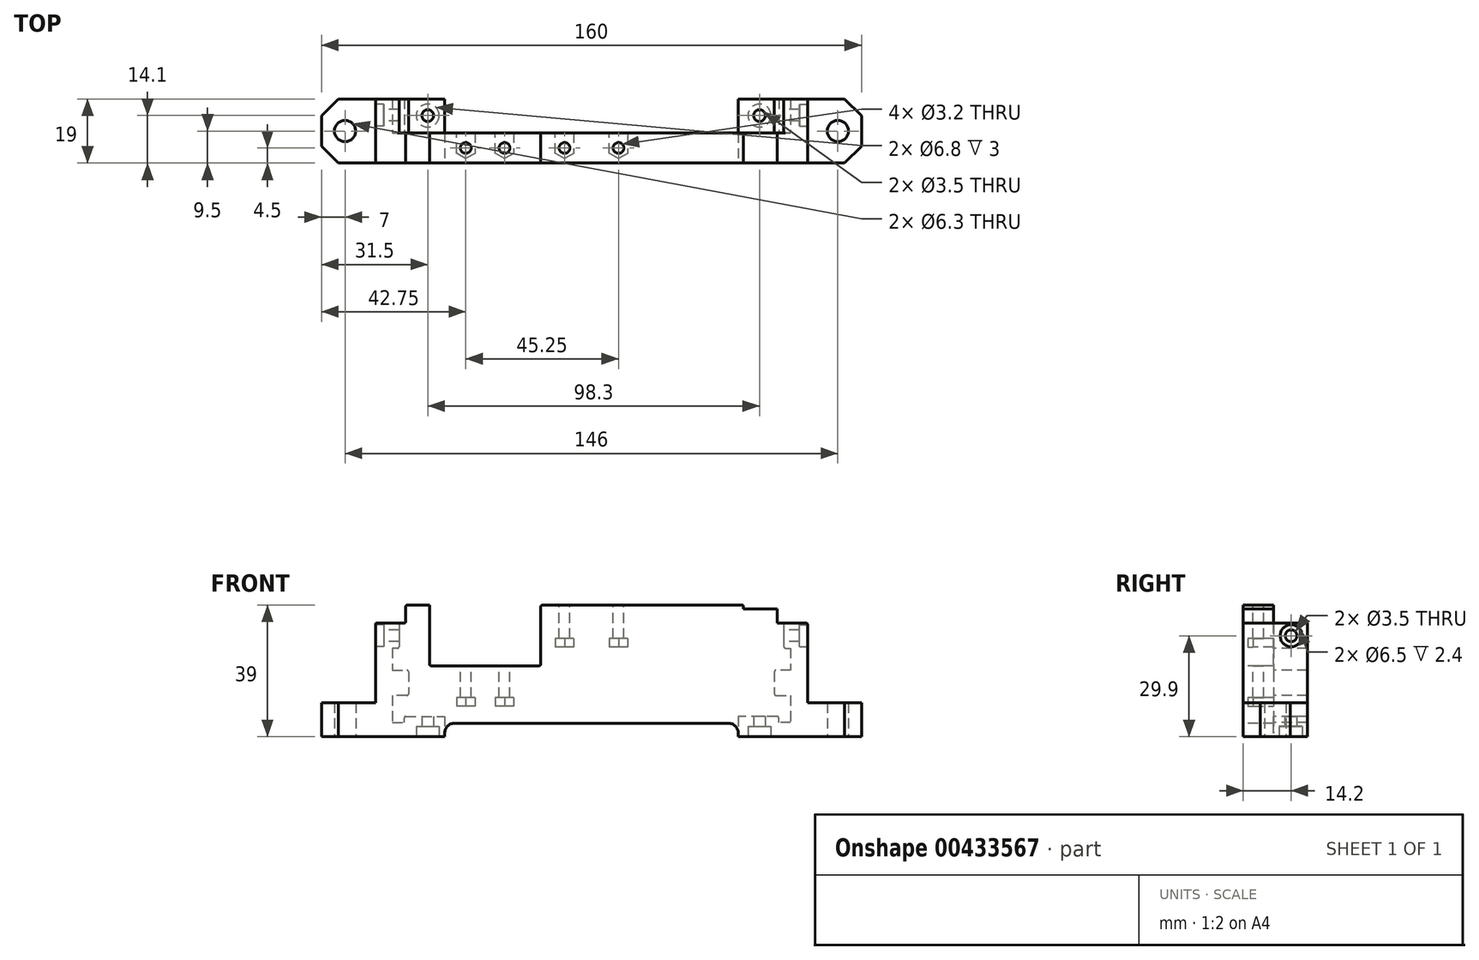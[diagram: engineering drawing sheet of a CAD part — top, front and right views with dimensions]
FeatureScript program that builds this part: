
annotation { "Feature Type Name" : "Feature", "Feature Type Description" : "" }
export const myFeature = defineFeature(function(context is Context, id is Id, definition is map)
    precondition{}
    {
        {
            var Q0;
            Q0=qCreatedBy(makeId("Front.planeOp"),FACE);
            var sketch = newSketch(context, id + "F0", { "sketchPlane" : qUnion([Q0])});
            skLineSegment(sketch, "E0", {"start": v(-64, 27.7) * mm, "end": v(-57.5, 27.7) * mm});
            skLineSegment(sketch, "E1", {"start": v(-57, 27.2) * mm, "end": v(-57, 20.7) * mm});
            skLineSegment(sketch, "E2", {"start": v(-57.5, 20.2) * mm, "end": v(-59, 20.2) * mm});
            skLineSegment(sketch, "E3", {"start": v(-59, 20.2) * mm, "end": v(-59, 13.7) * mm});
            skLineSegment(sketch, "E4", {"start": v(-59, 13.7) * mm, "end": v(-54.7, 13.7) * mm});
            skLineSegment(sketch, "E5", {"start": v(-54.2, 13.2) * mm, "end": v(-54.2, 6.7) * mm});
            skLineSegment(sketch, "E6", {"start": v(-54.7, 6.2) * mm, "end": v(-59, 6.2) * mm});
            skLineSegment(sketch, "E7", {"start": v(-59, 6.2) * mm, "end": v(-59, -1.8) * mm});
            skLineSegment(sketch, "E8", {"start": v(-59, -1.8) * mm, "end": v(-55.5, -1.8) * mm});
            skLineSegment(sketch, "E9", {"start": v(-55.5, -1.8) * mm, "end": v(-55.5, -0.5) * mm});
            skLineSegment(sketch, "E10", {"start": v(-55, 0) * mm, "end": v(-43.5, 0) * mm});
            skLineSegment(sketch, "E11", {"start": v(-43.5, 0) * mm, "end": v(-43.5, -6) * mm});
            skLineSegment(sketch, "E12", {"start": v(-43.5, -6) * mm, "end": v(-64, -6) * mm});
            skLineSegment(sketch, "E13", {"start": v(-64, -6) * mm, "end": v(-64, 27.7) * mm});
            skLineSegment(sketch, "E14", {"start": v(0, 0) * mm, "end": v(0, 39.92) * mm, "construction": true});
            skPoint(sketch, "E15.visualSharp", {"position": v(-54.2, 13.7) * mm});
            skArc(sketch, "E15.filletArc", {"start": v(-54.2, 13.2) * mm, "mid": v(-54.35, 13.55) * mm, "end": v(-54.7, 13.7) * mm});
            skPoint(sketch, "E16.visualSharp", {"position": v(-54.2, 6.2) * mm});
            skArc(sketch, "E16.filletArc", {"start": v(-54.7, 6.2) * mm, "mid": v(-54.35, 6.35) * mm, "end": v(-54.2, 6.7) * mm});
            skPoint(sketch, "E17.visualSharp", {"position": v(-55.5, 0) * mm});
            skArc(sketch, "E17.filletArc", {"start": v(-55, 0) * mm, "mid": v(-55.35, -0.15) * mm, "end": v(-55.5, -0.5) * mm});
            skPoint(sketch, "E18.visualSharp", {"position": v(-57, 27.7) * mm});
            skArc(sketch, "E18.filletArc", {"start": v(-57, 27.2) * mm, "mid": v(-57.15, 27.55) * mm, "end": v(-57.5, 27.7) * mm});
            skPoint(sketch, "E19.visualSharp", {"position": v(-57, 20.2) * mm});
            skArc(sketch, "E19.filletArc", {"start": v(-57.5, 20.2) * mm, "mid": v(-57.15, 20.35) * mm, "end": v(-57, 20.7) * mm});
            skLineSegment(sketch, "E20.MirrorCS", {"start": v(64, -6) * mm, "end": v(64, 27.7) * mm});
            skLineSegment(sketch, "E21.MirrorCS", {"start": v(43.5, -6) * mm, "end": v(64, -6) * mm});
            skLineSegment(sketch, "E22.MirrorCS", {"start": v(43.5, 0) * mm, "end": v(43.5, -6) * mm});
            skLineSegment(sketch, "E23.MirrorCS", {"start": v(55, 0) * mm, "end": v(43.5, 0) * mm});
            skArc(sketch, "E24.MirrorCS", {"start": v(55, 0) * mm, "mid": v(55.35, -0.15) * mm, "end": v(55.5, -0.5) * mm});
            skLineSegment(sketch, "E25.MirrorCS", {"start": v(55.5, -1.8) * mm, "end": v(55.5, -0.5) * mm});
            skLineSegment(sketch, "E26.MirrorCS", {"start": v(59, -1.8) * mm, "end": v(55.5, -1.8) * mm});
            skLineSegment(sketch, "E27.MirrorCS", {"start": v(59, 6.2) * mm, "end": v(59, -1.8) * mm});
            skLineSegment(sketch, "E28.MirrorCS", {"start": v(54.7, 6.2) * mm, "end": v(59, 6.2) * mm});
            skArc(sketch, "E29.MirrorCS", {"start": v(54.7, 6.2) * mm, "mid": v(54.35, 6.35) * mm, "end": v(54.2, 6.7) * mm});
            skLineSegment(sketch, "E30.MirrorCS", {"start": v(54.2, 13.2) * mm, "end": v(54.2, 6.7) * mm});
            skArc(sketch, "E31.MirrorCS", {"start": v(54.2, 13.2) * mm, "mid": v(54.35, 13.55) * mm, "end": v(54.7, 13.7) * mm});
            skLineSegment(sketch, "E32.MirrorCS", {"start": v(59, 13.7) * mm, "end": v(54.7, 13.7) * mm});
            skLineSegment(sketch, "E33.MirrorCS", {"start": v(59, 20.2) * mm, "end": v(59, 13.7) * mm});
            skLineSegment(sketch, "E34.MirrorCS", {"start": v(57.5, 20.2) * mm, "end": v(59, 20.2) * mm});
            skArc(sketch, "E35.MirrorCS", {"start": v(57.5, 20.2) * mm, "mid": v(57.15, 20.35) * mm, "end": v(57, 20.7) * mm});
            skLineSegment(sketch, "E36.MirrorCS", {"start": v(57, 27.2) * mm, "end": v(57, 20.7) * mm});
            skArc(sketch, "E37.MirrorCS", {"start": v(57, 27.2) * mm, "mid": v(57.15, 27.55) * mm, "end": v(57.5, 27.7) * mm});
            skLineSegment(sketch, "E38.MirrorCS", {"start": v(64, 27.7) * mm, "end": v(57.5, 27.7) * mm});
            skSolve(sketch);
        }
        {
            var Q0;
            Q0=makeQuery(id+"F0.imprint","IMPRINT",FACE,{"disambiguationData":[TD([[makeQuery(id+"F0.imprint","IMPRINT",EDGE,{"derivedFrom":sQuery(id+"F0.wireOp",EDGE,"E0")}),-1.0]])]});
            var sketch = newSketch(context, id + "F1", { "sketchPlane" : qUnion([Q0])});
            skLineSegment(sketch, "E39", {"start": v(-64, 27.7) * mm, "end": v(-64, -6) * mm});
            skLineSegment(sketch, "E40", {"start": v(-64, -6) * mm, "end": v(0, -6) * mm});
            skLineSegment(sketch, "E41", {"start": v(-64, 27.7) * mm, "end": v(-55, 27.7) * mm});
            skLineSegment(sketch, "E42", {"start": v(-55, 27.7) * mm, "end": v(-55, 31.9) * mm});
            skLineSegment(sketch, "E43", {"start": v(-55, 31.9) * mm, "end": v(0, 31.9) * mm});
            skLineSegment(sketch, "E44.MirrorCS", {"start": v(55, 31.9) * mm, "end": v(0, 31.9) * mm});
            skLineSegment(sketch, "E45.MirrorCS", {"start": v(64, -6) * mm, "end": v(0, -6) * mm});
            skLineSegment(sketch, "E46.MirrorCS", {"start": v(64, 27.7) * mm, "end": v(64, -6) * mm});
            skLineSegment(sketch, "E47.MirrorCS", {"start": v(64, 27.7) * mm, "end": v(55, 27.7) * mm});
            skLineSegment(sketch, "E48.MirrorCS", {"start": v(55, 27.7) * mm, "end": v(55, 31.9) * mm});
            skSolve(sketch);
        }
        {
            var Q0;
            Q0=qSketchRegion(id+"F1",true);
            extrude(context, id + "F2", {"entities" : qUnion([Q0]), "depth" : 9 * mm});
        }
        {
            var Q0;
            Q0=qSketchRegion(id+"F0",true);
            extrude(context, id + "F3", {"entities" : qUnion([Q0]), "operationType" : NewBodyOperationType.ADD, "oppositeDirection" : true, "depth" : 10 * mm});
        }
        {
            var Q0;
            Q0=makeQuery(id+"F3.boolean.opBoolean","MERGE",FACE,{"derivedFrom":[makeQuery(id+"F2.opExtrude","SWEPT_FACE",FACE,{"disambiguationData":[OSD([sQuery(id+"F1.wireOp",EDGE,"E39")])]}),makeQuery(id+"F3.opExtrude","SWEPT_FACE",FACE,{"disambiguationData":[OSD([sQuery(id+"F0.wireOp",EDGE,"E13")])]})]});
            var sketch = newSketch(context, id + "F4", { "sketchPlane" : qUnion([Q0])});
            skCircle(sketch, "E49", {"center": v(-5.2, 23.9) * mm, "radius": 1.75 * mm});
            skCircle(sketch, "E50", {"center": v(-5.2, 23.9) * mm, "radius": 3.25 * mm});
            skSolve(sketch);
        }
        {
            var Q0;
            Q0=makeQuery(id+"F4.imprint","IMPRINT",FACE,{"disambiguationData":[TD([[makeQuery(id+"F4.imprint","IMPRINT",EDGE,{"derivedFrom":sQuery(id+"F4.wireOp",EDGE,"E49")}),1.0]])]});
            extrude(context, id + "F5", {"entities" : qUnion([Q0]), "operationType" : NewBodyOperationType.REMOVE, "oppositeDirection" : true, "depth" : 158.2 * mm});
        }
        {
            var Q0;
            Q0=makeQuery(id+"F4.imprint","IMPRINT",FACE,{"disambiguationData":[TD([[makeQuery(id+"F4.imprint","IMPRINT",EDGE,{"derivedFrom":sQuery(id+"F4.wireOp",EDGE,"E49")}),-1.0]])]});
            extrude(context, id + "F6", {"entities" : qUnion([Q0]), "operationType" : NewBodyOperationType.REMOVE, "oppositeDirection" : true, "depth" : 2.4 * mm});
        }
        {
            var Q0;
            Q0=makeQuery(id+"F3.boolean.opBoolean","MERGE",FACE,{"derivedFrom":[makeQuery(id+"F2.opExtrude","SWEPT_FACE",FACE,{"disambiguationData":[OSD([sQuery(id+"F1.wireOp",EDGE,"E46.MirrorCS")])]}),makeQuery(id+"F3.opExtrude","SWEPT_FACE",FACE,{"disambiguationData":[OSD([sQuery(id+"F0.wireOp",EDGE,"E20.MirrorCS")])]})]});
            var sketch = newSketch(context, id + "F7", { "sketchPlane" : qUnion([Q0])});
            skCircle(sketch, "E51", {"center": v(5.2, 23.9) * mm, "radius": 3.25 * mm});
            skSolve(sketch);
        }
        {
            var Q0;
            Q0=qSketchRegion(id+"F7",true);
            extrude(context, id + "F8", {"entities" : qUnion([Q0]), "operationType" : NewBodyOperationType.REMOVE, "oppositeDirection" : true, "depth" : 2.4 * mm});
        }
        {
            var Q0;
            Q0=makeQuery(id+"F3.boolean.opBoolean","MERGE",FACE,{"derivedFrom":[makeQuery(id+"F2.opExtrude","SWEPT_FACE",FACE,{"disambiguationData":[OSD([sQuery(id+"F1.wireOp",EDGE,"E40"),sQuery(id+"F1.wireOp",EDGE,"E45.MirrorCS")])]}),makeQuery(id+"F3.opExtrude","SWEPT_FACE",FACE,{"disambiguationData":[OSD([sQuery(id+"F0.wireOp",EDGE,"E12")])]}),makeQuery(id+"F3.opExtrude","SWEPT_FACE",FACE,{"disambiguationData":[OSD([sQuery(id+"F0.wireOp",EDGE,"E21.MirrorCS")])]})]});
            var sketch = newSketch(context, id + "F9", { "sketchPlane" : qUnion([Q0])});
            skCircle(sketch, "E52", {"center": v(49.8, -5.1) * mm, "radius": 1.75 * mm});
            skCircle(sketch, "E53", {"center": v(49.8, -5.1) * mm, "radius": 3.4 * mm});
            skCircle(sketch, "E54", {"center": v(-48.5, -5.1) * mm, "radius": 1.75 * mm});
            skCircle(sketch, "E55", {"center": v(-48.5, -5.1) * mm, "radius": 3.4 * mm});
            skSolve(sketch);
        }
        {
            var Q0;
            Q0=qSketchRegion(id+"F9",true);
            var Q1;
            Q1=makeQuery(id+"F9.imprint","IMPRINT",FACE,{"disambiguationData":[TD([[makeQuery(id+"F9.imprint","IMPRINT",EDGE,{"derivedFrom":sQuery(id+"F9.wireOp",EDGE,"E52")}),1.0]])]});
            extrude(context, id + "F10", {"entities" : qUnion([Q0, Q1]), "operationType" : NewBodyOperationType.REMOVE, "oppositeDirection" : true, "depth" : 3 * mm});
        }
        {
            var Q0;
            Q0=makeQuery(id+"F9.imprint","IMPRINT",FACE,{"disambiguationData":[TD([[makeQuery(id+"F9.imprint","IMPRINT",EDGE,{"derivedFrom":sQuery(id+"F9.wireOp",EDGE,"E52")}),1.0]])]});
            var Q1;
            Q1=makeQuery(id+"F9.imprint","IMPRINT",FACE,{"disambiguationData":[TD([[makeQuery(id+"F9.imprint","IMPRINT",EDGE,{"derivedFrom":sQuery(id+"F9.wireOp",EDGE,"E54")}),1.0]])]});
            extrude(context, id + "F11", {"entities" : qUnion([Q0, Q1]), "operationType" : NewBodyOperationType.REMOVE, "oppositeDirection" : true, "depth" : 25 * mm});
        }
        {
            var Q0;
            Q0=makeQuery(id+"F2.opExtrude","SWEPT_FACE",FACE,{"disambiguationData":[OSD([sQuery(id+"F1.wireOp",EDGE,"E43"),sQuery(id+"F1.wireOp",EDGE,"E44.MirrorCS")])]});
            var sketch = newSketch(context, id + "F12", { "sketchPlane" : qUnion([Q0])});
            skLineSegment(sketch, "E56.bottom", {"start": v(45, -9) * mm, "end": v(-55, -9) * mm});
            skLineSegment(sketch, "E56.top", {"start": v(45, 0) * mm, "end": v(-55, 0) * mm});
            skLineSegment(sketch, "E56.left", {"start": v(45, -9) * mm, "end": v(45, 0) * mm});
            skLineSegment(sketch, "E56.right", {"start": v(-55, -9) * mm, "end": v(-55, 0) * mm});
            skSolve(sketch);
        }
        {
            var Q0;
            Q0=qSketchRegion(id+"F12",true);
            extrude(context, id + "F13", {"entities" : qUnion([Q0]), "operationType" : NewBodyOperationType.ADD, "depth" : 1.1 * mm});
        }
        {
            var Q0;
            Q0=makeQuery(id+"F4.imprint","IMPRINT",FACE,{"disambiguationData":[TD([[makeQuery(id+"F4.imprint","IMPRINT",EDGE,{"derivedFrom":sQuery(id+"F4.wireOp",EDGE,"E50")}),-1.0]])]});
            var sketch = newSketch(context, id + "F14", { "sketchPlane" : qUnion([Q0])});
            skLineSegment(sketch, "E57.bottom", {"start": v(9, -6) * mm, "end": v(-10, -6) * mm});
            skLineSegment(sketch, "E57.top", {"start": v(9, 4) * mm, "end": v(-10, 4) * mm});
            skLineSegment(sketch, "E57.left", {"start": v(9, -6) * mm, "end": v(9, 4) * mm});
            skLineSegment(sketch, "E57.right", {"start": v(-10, -6) * mm, "end": v(-10, 4) * mm});
            skSolve(sketch);
        }
        {
            var Q0;
            Q0=qSketchRegion(id+"F14",true);
            extrude(context, id + "F15", {"entities" : qUnion([Q0]), "operationType" : NewBodyOperationType.ADD, "depth" : 16 * mm});
        }
        {
            var Q0;
            Q0=makeQuery(id+"F15.opExtrude","CAP_EDGE",EDGE,{"disambiguationData":[OSD([sQuery(id+"F14.wireOp",EDGE,"E57.left")])],"isStart":false});
            var Q1;
            Q1=makeQuery(id+"F15.opExtrude","CAP_EDGE",EDGE,{"disambiguationData":[OSD([sQuery(id+"F14.wireOp",EDGE,"E57.right")])],"isStart":false});
            chamfer(context, id + "F16", {"entities" : qUnion([Q0, Q1]), "width" : 5 * mm, "tangentPropagation" : true});
        }
        {
            var Q0;
            Q0=makeQuery(id+"F3.boolean.opBoolean","MERGE",FACE,{"derivedFrom":[makeQuery(id+"F2.opExtrude","SWEPT_FACE",FACE,{"disambiguationData":[OSD([sQuery(id+"F1.wireOp",EDGE,"E46.MirrorCS")])]}),makeQuery(id+"F3.opExtrude","SWEPT_FACE",FACE,{"disambiguationData":[OSD([sQuery(id+"F0.wireOp",EDGE,"E20.MirrorCS")])]})]});
            var sketch = newSketch(context, id + "F17", { "sketchPlane" : qUnion([Q0])});
            skLineSegment(sketch, "E58.bottom", {"start": v(-9, -6) * mm, "end": v(10, -6) * mm});
            skLineSegment(sketch, "E58.top", {"start": v(-9, 4) * mm, "end": v(10, 4) * mm});
            skLineSegment(sketch, "E58.left", {"start": v(-9, -6) * mm, "end": v(-9, 4) * mm});
            skLineSegment(sketch, "E58.right", {"start": v(10, -6) * mm, "end": v(10, 4) * mm});
            skSolve(sketch);
        }
        {
            var Q0;
            Q0=qSketchRegion(id+"F17",true);
            extrude(context, id + "F18", {"entities" : qUnion([Q0]), "operationType" : NewBodyOperationType.ADD, "depth" : 16 * mm});
        }
        {
            var Q0;
            Q0=makeQuery(id+"F18.opExtrude","CAP_EDGE",EDGE,{"disambiguationData":[OSD([sQuery(id+"F17.wireOp",EDGE,"E58.right")])],"isStart":false});
            var Q1;
            Q1=makeQuery(id+"F18.opExtrude","CAP_EDGE",EDGE,{"disambiguationData":[OSD([sQuery(id+"F17.wireOp",EDGE,"E58.left")])],"isStart":false});
            chamfer(context, id + "F19", {"entities" : qUnion([Q0, Q1]), "width" : 5 * mm, "tangentPropagation" : true});
        }
        {
            var Q0;
            {var subQ1=sQuery(id+"F0.wireOp",EDGE,"E21.MirrorCS");var subQ7=sQuery(id+"F1.wireOp",EDGE,"E45.MirrorCS");var subQ12=sQuery(id+"F1.wireOp",EDGE,"E40");var subQ13=sQuery(id+"F1.wireOp",EDGE,"E39");var subQ15=sQuery(id+"F0.wireOp",EDGE,"E12");Q0=makeQuery(id+"F18.boolean.opBoolean","MERGE",FACE,{"derivedFrom":[makeQuery(id+"F15.boolean.opBoolean","MERGE",FACE,{"derivedFrom":[makeQuery(id+"F10.boolean.opBoolean","SPLIT",FACE,{"disambiguationData":[TD([makeQuery(id+"F2.opExtrude","SWEPT_FACE",FACE,{"disambiguationData":[OSD([subQ13])]})])],"derivedFrom":makeQuery(id+"F3.boolean.opBoolean","MERGE",FACE,{"derivedFrom":[makeQuery(id+"F2.opExtrude","SWEPT_FACE",FACE,{"disambiguationData":[OSD([subQ12,subQ7])]}),makeQuery(id+"F3.opExtrude","SWEPT_FACE",FACE,{"disambiguationData":[OSD([subQ15])]}),makeQuery(id+"F3.opExtrude","SWEPT_FACE",FACE,{"disambiguationData":[OSD([subQ1])]})]})}),makeQuery(id+"F15.opExtrude","SWEPT_FACE",FACE,{"disambiguationData":[OSD([sQuery(id+"F14.wireOp",EDGE,"E57.bottom")])]})]}),makeQuery(id+"F18.opExtrude","SWEPT_FACE",FACE,{"disambiguationData":[OSD([sQuery(id+"F17.wireOp",EDGE,"E58.bottom")])]})]});}
            var sketch = newSketch(context, id + "F20", { "sketchPlane" : qUnion([Q0])});
            skCircle(sketch, "E59", {"center": v(-73, -0.5) * mm, "radius": 3.15 * mm});
            skPoint(sketch, "E59.centerSnap0", {"position": v(-80, -0.5) * mm});
            skCircle(sketch, "E60", {"center": v(73, -0.5) * mm, "radius": 3.15 * mm});
            skPoint(sketch, "E60.centerSnap0", {"position": v(80, -0.5) * mm});
            skSolve(sketch);
        }
        {
            var Q0;
            Q0=qSketchRegion(id+"F20",true);
            extrude(context, id + "F21", {"entities" : qUnion([Q0]), "operationType" : NewBodyOperationType.REMOVE, "oppositeDirection" : true, "depth" : 25 * mm});
        }
        {
            var Q0;
            Q0=makeQuery(id+"F3.boolean.opBoolean","MERGE",EDGE,{"derivedFrom":[makeQuery(id+"F2.opExtrude","SWEPT_EDGE",EDGE,{"disambiguationData":[OSD([sQuery(id+"F1.wireOp",EDGE,"E46.MirrorCS"),sQuery(id+"F1.wireOp",EDGE,"E47.MirrorCS")])]}),makeQuery(id+"F3.opExtrude","SWEPT_EDGE",EDGE,{"disambiguationData":[OSD([sQuery(id+"F0.wireOp",EDGE,"E20.MirrorCS"),sQuery(id+"F0.wireOp",EDGE,"E38.MirrorCS")])]})]});
            var Q1;
            Q1=makeQuery(id+"F13.opExtrude","CAP_EDGE",EDGE,{"disambiguationData":[OSD([sQuery(id+"F12.wireOp",EDGE,"E56.left")])],"isStart":false});
            var Q2;
            Q2=makeQuery(id+"F3.boolean.opBoolean","MERGE",EDGE,{"derivedFrom":[makeQuery(id+"F2.opExtrude","SWEPT_EDGE",EDGE,{"disambiguationData":[OSD([sQuery(id+"F1.wireOp",EDGE,"E39"),sQuery(id+"F1.wireOp",EDGE,"E41")])]}),makeQuery(id+"F3.opExtrude","SWEPT_EDGE",EDGE,{"disambiguationData":[OSD([sQuery(id+"F0.wireOp",EDGE,"E0"),sQuery(id+"F0.wireOp",EDGE,"E13")])]})]});
            var Q3;
            Q3=makeQuery(id+"F2.opExtrude","SWEPT_EDGE",EDGE,{"disambiguationData":[OSD([sQuery(id+"F1.wireOp",EDGE,"E41"),sQuery(id+"F1.wireOp",EDGE,"E42")])]});
            var Q4;
            Q4=makeQuery(id+"F2.opExtrude","SWEPT_EDGE",EDGE,{"disambiguationData":[OSD([sQuery(id+"F1.wireOp",EDGE,"E42"),sQuery(id+"F1.wireOp",EDGE,"E43")])]});
            var Q5;
            Q5=makeQuery(id+"F13.opExtrude","CAP_EDGE",EDGE,{"disambiguationData":[OSD([sQuery(id+"F12.wireOp",EDGE,"E56.right")])],"isStart":true});
            var Q6;
            Q6=makeQuery(id+"F13.opExtrude","CAP_EDGE",EDGE,{"disambiguationData":[OSD([sQuery(id+"F12.wireOp",EDGE,"E56.right")])],"isStart":false});
            var Q7;
            Q7=makeQuery(id+"F15.opExtrude","CAP_EDGE",EDGE,{"disambiguationData":[OSD([sQuery(id+"F14.wireOp",EDGE,"E57.top")])],"isStart":true});
            var Q8;
            Q8=makeQuery(id+"F18.opExtrude","CAP_EDGE",EDGE,{"disambiguationData":[OSD([sQuery(id+"F17.wireOp",EDGE,"E58.top")])],"isStart":true});
            fillet(context, id + "F22", {"entities" : qUnion([Q0, Q1, Q2, Q3, Q4, Q5, Q6, Q7, Q8]), "radius" : 0.4 * mm, "tangentPropagation" : true, "allowEdgeOverflow" : false});
        }
        {
            var Q0;
            Q0=makeQuery(id+"F9.imprint","IMPRINT",FACE,{"disambiguationData":[TD([[makeQuery(id+"F9.imprint","IMPRINT",EDGE,{"derivedFrom":sQuery(id+"F9.wireOp",EDGE,"E53")}),-1.0]])]});
            var sketch = newSketch(context, id + "F23", { "sketchPlane" : qUnion([Q0])});
            skLineSegment(sketch, "E61.bottom", {"start": v(-43.5, 0) * mm, "end": v(43.5, 0) * mm});
            skLineSegment(sketch, "E61.top", {"start": v(-43.5, 9) * mm, "end": v(43.5, 9) * mm});
            skLineSegment(sketch, "E61.left", {"start": v(-43.5, 0) * mm, "end": v(-43.5, 9) * mm});
            skLineSegment(sketch, "E61.right", {"start": v(43.5, 0) * mm, "end": v(43.5, 9) * mm});
            skSolve(sketch);
        }
        {
            var Q0;
            Q0=qSketchRegion(id+"F23",true);
            extrude(context, id + "F24", {"entities" : qUnion([Q0]), "operationType" : NewBodyOperationType.REMOVE, "oppositeDirection" : true, "depth" : 4 * mm});
        }
        {
            var Q0;
            Q0=makeQuery(id+"F24.boolean.opBoolean","COPY",EDGE,{"derivedFrom":makeQuery(id+"F24.opExtrude","CAP_EDGE",EDGE,{"disambiguationData":[OSD([sQuery(id+"F23.wireOp",EDGE,"E61.left")])],"isStart":false})});
            var Q1;
            Q1=makeQuery(id+"F24.boolean.opBoolean","COPY",EDGE,{"derivedFrom":makeQuery(id+"F24.opExtrude","CAP_EDGE",EDGE,{"disambiguationData":[OSD([sQuery(id+"F23.wireOp",EDGE,"E61.right")])],"isStart":false})});
            fillet(context, id + "F25", {"entities" : qUnion([Q0, Q1]), "radius" : 3 * mm, "tangentPropagation" : true, "allowEdgeOverflow" : false});
        }
        {
            var Q0;
            Q0=makeQuery(id+"F13.opExtrude","CAP_FACE",FACE,{"disambiguationData":[OSD([sQuery(id+"F12.wireOp",EDGE,"E56.bottom"),sQuery(id+"F12.wireOp",EDGE,"E56.top"),sQuery(id+"F12.wireOp",EDGE,"E56.left"),sQuery(id+"F12.wireOp",EDGE,"E56.right")])],"isStart":false});
            var sketch = newSketch(context, id + "F26", { "sketchPlane" : qUnion([Q0])});
            skLineSegment(sketch, "E62.bottom", {"start": v(-48, 0) * mm, "end": v(-15, 0) * mm});
            skLineSegment(sketch, "E62.top", {"start": v(-48, -9) * mm, "end": v(-15, -9) * mm});
            skLineSegment(sketch, "E62.left", {"start": v(-48, 0) * mm, "end": v(-48, -9) * mm});
            skLineSegment(sketch, "E62.right", {"start": v(-15, 0) * mm, "end": v(-15, -9) * mm});
            skCircle(sketch, "E63", {"center": v(-37.25, -4.5) * mm, "radius": 1.6 * mm});
            skPoint(sketch, "E63.centerSnap0", {"position": v(-15, -4.5) * mm});
            skCircle(sketch, "E64", {"center": v(-25.75, -4.5) * mm, "radius": 1.6 * mm});
            skLineSegment(sketch, "E65", {"start": v(-37.25, -4.5) * mm, "end": v(-25.75, -4.5) * mm, "construction": true});
            skLineSegment(sketch, "E66", {"start": v(-31.5, -2.87) * mm, "end": v(-31.5, -5.86) * mm, "construction": true});
            skPoint(sketch, "E66.startSnap0", {"position": v(-31.5, -4.5) * mm});
            skSolve(sketch);
        }
        {
            var Q0;
            Q0=makeQuery(id+"F26.imprint","IMPRINT",FACE,{"disambiguationData":[TD([[makeQuery(id+"F26.imprint","IMPRINT",EDGE,{"derivedFrom":sQuery(id+"F26.wireOp",EDGE,"E62.bottom")}),1.0]])]});
            extrude(context, id + "F27", {"entities" : qUnion([Q0]), "operationType" : NewBodyOperationType.REMOVE, "oppositeDirection" : true, "depth" : 18 * mm});
        }
        {
            var Q0;
            Q0=makeQuery(id+"F26.imprint","IMPRINT",FACE,{"disambiguationData":[TD([[makeQuery(id+"F26.imprint","IMPRINT",EDGE,{"derivedFrom":sQuery(id+"F26.wireOp",EDGE,"E63")}),1.0]])]});
            var Q1;
            Q1=makeQuery(id+"F26.imprint","IMPRINT",FACE,{"disambiguationData":[TD([[makeQuery(id+"F26.imprint","IMPRINT",EDGE,{"derivedFrom":sQuery(id+"F26.wireOp",EDGE,"E64")}),1.0]])]});
            extrude(context, id + "F28", {"entities" : qUnion([Q0, Q1]), "operationType" : NewBodyOperationType.REMOVE, "oppositeDirection" : true, "depth" : 30 * mm});
        }
        {
            var Q0;
            Q0=makeQuery(id+"F28.boolean.opBoolean","COPY",FACE,{"derivedFrom":makeQuery(id+"F28.opExtrude","CAP_FACE",FACE,{"disambiguationData":[OSD([sQuery(id+"F26.wireOp",EDGE,"E64")])],"isStart":false})});
            var sketch = newSketch(context, id + "F29", { "sketchPlane" : qUnion([Q0])});
            skCircle(sketch, "E67.cCircle", {"center": v(-25.75, -4.5) * mm, "radius": 2.75 * mm, "construction": true});
            skLineSegment(sketch, "E67.0", {"start": v(-28.5, -6.09) * mm, "end": v(-28.5, -2.91) * mm});
            skLineSegment(sketch, "E67.1", {"start": v(-28.5, -2.91) * mm, "end": v(-25.75, -1.32) * mm});
            skLineSegment(sketch, "E67.2", {"start": v(-25.75, -1.32) * mm, "end": v(-23, -2.91) * mm});
            skLineSegment(sketch, "E67.3", {"start": v(-23, -2.91) * mm, "end": v(-23, -6.09) * mm});
            skLineSegment(sketch, "E67.4", {"start": v(-23, -6.09) * mm, "end": v(-25.75, -7.68) * mm});
            skLineSegment(sketch, "E67.5", {"start": v(-25.75, -7.68) * mm, "end": v(-28.5, -6.09) * mm});
            skPoint(sketch, "E67.0.midPoint", {"position": v(-28.5, -4.5) * mm});
            skCircle(sketch, "E68.cCircle", {"center": v(-37.25, -4.5) * mm, "radius": 2.75 * mm, "construction": true});
            skLineSegment(sketch, "E68.0", {"start": v(-40, -6.09) * mm, "end": v(-40, -2.91) * mm});
            skLineSegment(sketch, "E68.1", {"start": v(-40, -2.91) * mm, "end": v(-37.25, -1.32) * mm});
            skLineSegment(sketch, "E68.2", {"start": v(-37.25, -1.32) * mm, "end": v(-34.5, -2.91) * mm});
            skLineSegment(sketch, "E68.3", {"start": v(-34.5, -2.91) * mm, "end": v(-34.5, -6.09) * mm});
            skLineSegment(sketch, "E68.4", {"start": v(-34.5, -6.09) * mm, "end": v(-37.25, -7.68) * mm});
            skLineSegment(sketch, "E68.5", {"start": v(-37.25, -7.68) * mm, "end": v(-40, -6.09) * mm});
            skPoint(sketch, "E68.0.midPoint", {"position": v(-40, -4.5) * mm});
            skSolve(sketch);
        }
        {
            var Q0;
            Q0 = qSketchRegion(id + "F29", true);
            extrude(context, id + "F30", {"entities" : qUnion([Q0]), "operationType" : NewBodyOperationType.REMOVE, "depth" : 2.6 * mm});
        }
        {
            var Q0;
            {var subQ0=sQuery(id+"F12.wireOp",EDGE,"E56.top");var subQ11=sQuery(id+"F12.wireOp",EDGE,"E56.bottom");var subQ12=sQuery(id+"F12.wireOp",EDGE,"E56.left");Q0=makeQuery(id+"F27.boolean.opBoolean","SPLIT",FACE,{"disambiguationData":[TD([makeQuery(id+"F22.opFillet","BLEND_FACE",FACE,{"disambiguationData":[OSD([subQ12])]})])],"derivedFrom":makeQuery(id+"F13.opExtrude","CAP_FACE",FACE,{"disambiguationData":[OSD([subQ11,subQ0,subQ12,sQuery(id+"F12.wireOp",EDGE,"E56.right")])],"isStart":false})});}
            var sketch = newSketch(context, id + "F31", { "sketchPlane" : qUnion([Q0])});
            skCircle(sketch, "E69", {"center": v(-8, -4.5) * mm, "radius": 1.6 * mm});
            skPoint(sketch, "E69.centerSnap0", {"position": v(-15, -4.5) * mm});
            skCircle(sketch, "E70", {"center": v(8, -4.5) * mm, "radius": 1.6 * mm});
            skSolve(sketch);
        }
        {
            var Q0;
            Q0=makeQuery(id+"F31.imprint","IMPRINT",FACE,{"disambiguationData":[TD([[makeQuery(id+"F31.imprint","IMPRINT",EDGE,{"derivedFrom":sQuery(id+"F31.wireOp",EDGE,"E69")}),1.0]])]});
            var Q1;
            Q1=makeQuery(id+"F31.imprint","IMPRINT",FACE,{"disambiguationData":[TD([[makeQuery(id+"F31.imprint","IMPRINT",EDGE,{"derivedFrom":sQuery(id+"F31.wireOp",EDGE,"E70")}),1.0]])]});
            extrude(context, id + "F32", {"entities" : qUnion([Q0, Q1]), "operationType" : NewBodyOperationType.REMOVE, "oppositeDirection" : true, "depth" : 12.5 * mm});
        }
        {
            var Q0;
            Q0=makeQuery(id+"F32.boolean.opBoolean","COPY",FACE,{"derivedFrom":makeQuery(id+"F32.opExtrude","CAP_FACE",FACE,{"disambiguationData":[OSD([sQuery(id+"F31.wireOp",EDGE,"E69")])],"isStart":false})});
            var sketch = newSketch(context, id + "F33", { "sketchPlane" : qUnion([Q0])});
            skCircle(sketch, "E71.cCircle", {"center": v(-8, -4.5) * mm, "radius": 2.75 * mm, "construction": true});
            skLineSegment(sketch, "E71.0", {"start": v(-5.25, -2.91) * mm, "end": v(-5.25, -6.09) * mm});
            skLineSegment(sketch, "E71.1", {"start": v(-5.25, -6.09) * mm, "end": v(-8, -7.68) * mm});
            skLineSegment(sketch, "E71.2", {"start": v(-8, -7.68) * mm, "end": v(-10.75, -6.09) * mm});
            skLineSegment(sketch, "E71.3", {"start": v(-10.75, -6.09) * mm, "end": v(-10.75, -2.91) * mm});
            skLineSegment(sketch, "E71.4", {"start": v(-10.75, -2.91) * mm, "end": v(-8, -1.32) * mm});
            skLineSegment(sketch, "E71.5", {"start": v(-8, -1.32) * mm, "end": v(-5.25, -2.91) * mm});
            skPoint(sketch, "E71.0.midPoint", {"position": v(-5.25, -4.5) * mm});
            skCircle(sketch, "E72.cCircle", {"center": v(8, -4.5) * mm, "radius": 2.75 * mm, "construction": true});
            skLineSegment(sketch, "E72.0", {"start": v(10.75, -2.91) * mm, "end": v(10.75, -6.09) * mm});
            skLineSegment(sketch, "E72.1", {"start": v(10.75, -6.09) * mm, "end": v(8, -7.68) * mm});
            skLineSegment(sketch, "E72.2", {"start": v(8, -7.68) * mm, "end": v(5.25, -6.09) * mm});
            skLineSegment(sketch, "E72.3", {"start": v(5.25, -6.09) * mm, "end": v(5.25, -2.91) * mm});
            skLineSegment(sketch, "E72.4", {"start": v(5.25, -2.91) * mm, "end": v(8, -1.32) * mm});
            skLineSegment(sketch, "E72.5", {"start": v(8, -1.32) * mm, "end": v(10.75, -2.91) * mm});
            skPoint(sketch, "E72.0.midPoint", {"position": v(10.75, -4.5) * mm});
            skSolve(sketch);
        }
        {
            var Q0;
            Q0 = qSketchRegion(id + "F33", true);
            extrude(context, id + "F34", {"entities" : qUnion([Q0]), "operationType" : NewBodyOperationType.REMOVE, "depth" : 2.6 * mm});
        }
        {
            var Q0;
            Q0=makeQuery(id+"F13.boolean.opBoolean","MERGE",FACE,{"derivedFrom":[makeQuery(id+"F2.opExtrude","CAP_FACE",FACE,{"disambiguationData":[OSD([sQuery(id+"F1.wireOp",EDGE,"E39"),sQuery(id+"F1.wireOp",EDGE,"E40"),sQuery(id+"F1.wireOp",EDGE,"E41"),sQuery(id+"F1.wireOp",EDGE,"E42"),sQuery(id+"F1.wireOp",EDGE,"E43"),sQuery(id+"F1.wireOp",EDGE,"E44.MirrorCS"),sQuery(id+"F1.wireOp",EDGE,"E45.MirrorCS"),sQuery(id+"F1.wireOp",EDGE,"E46.MirrorCS"),sQuery(id+"F1.wireOp",EDGE,"E47.MirrorCS"),sQuery(id+"F1.wireOp",EDGE,"E48.MirrorCS")])],"isStart":true}),makeQuery(id+"F13.opExtrude","SWEPT_FACE",FACE,{"disambiguationData":[OSD([sQuery(id+"F12.wireOp",EDGE,"E56.top")])]})]});
            var sketch = newSketch(context, id + "F35", { "sketchPlane" : qUnion([Q0])});
            skLineSegment(sketch, "E73.bottom", {"start": v(-10.75, 23.1) * mm, "end": v(-5.25, 23.1) * mm});
            skLineSegment(sketch, "E73.top", {"start": v(-10.75, 20.5) * mm, "end": v(-5.25, 20.5) * mm});
            skLineSegment(sketch, "E73.left", {"start": v(-10.75, 23.1) * mm, "end": v(-10.75, 20.5) * mm});
            skLineSegment(sketch, "E73.right", {"start": v(-5.25, 23.1) * mm, "end": v(-5.25, 20.5) * mm});
            skLineSegment(sketch, "E74.bottom", {"start": v(5.25, 23.1) * mm, "end": v(10.75, 23.1) * mm});
            skLineSegment(sketch, "E74.top", {"start": v(5.25, 20.5) * mm, "end": v(10.75, 20.5) * mm});
            skLineSegment(sketch, "E74.left", {"start": v(5.25, 23.1) * mm, "end": v(5.25, 20.5) * mm});
            skLineSegment(sketch, "E74.right", {"start": v(10.75, 23.1) * mm, "end": v(10.75, 20.5) * mm});
            skLineSegment(sketch, "E75.bottom", {"start": v(23, 5.6) * mm, "end": v(28.5, 5.6) * mm});
            skLineSegment(sketch, "E75.top", {"start": v(23, 3) * mm, "end": v(28.5, 3) * mm});
            skLineSegment(sketch, "E75.left", {"start": v(23, 5.6) * mm, "end": v(23, 3) * mm});
            skLineSegment(sketch, "E75.right", {"start": v(28.5, 5.6) * mm, "end": v(28.5, 3) * mm});
            skLineSegment(sketch, "E76.bottom", {"start": v(34.5, 5.6) * mm, "end": v(40, 5.6) * mm});
            skLineSegment(sketch, "E76.top", {"start": v(34.5, 3) * mm, "end": v(40, 3) * mm});
            skLineSegment(sketch, "E76.left", {"start": v(34.5, 5.6) * mm, "end": v(34.5, 3) * mm});
            skLineSegment(sketch, "E76.right", {"start": v(40, 5.6) * mm, "end": v(40, 3) * mm});
            skSolve(sketch);
        }
        {
            var Q0;
            Q0 = qSketchRegion(id + "F35", true);
            extrude(context, id + "F36", {"entities" : qUnion([Q0]), "operationType" : NewBodyOperationType.REMOVE, "oppositeDirection" : true, "depth" : 3.7 * mm});
        }
        {
            var Q0;
            Q0=makeQuery(id+"F27.boolean.opBoolean","COPY",EDGE,{"derivedFrom":makeQuery(id+"F27.opExtrude","CAP_EDGE",EDGE,{"disambiguationData":[OSD([sQuery(id+"F26.wireOp",EDGE,"E62.right")])],"isStart":true})});
            var Q1;
            Q1=makeQuery(id+"F27.boolean.opBoolean","COPY",EDGE,{"derivedFrom":makeQuery(id+"F27.opExtrude","CAP_EDGE",EDGE,{"disambiguationData":[OSD([sQuery(id+"F26.wireOp",EDGE,"E62.right")])],"isStart":false})});
            var Q2;
            Q2=makeQuery(id+"F27.boolean.opBoolean","COPY",EDGE,{"derivedFrom":makeQuery(id+"F27.opExtrude","CAP_EDGE",EDGE,{"disambiguationData":[OSD([sQuery(id+"F26.wireOp",EDGE,"E62.left")])],"isStart":false})});
            var Q3;
            Q3=makeQuery(id+"F27.boolean.opBoolean","COPY",EDGE,{"derivedFrom":makeQuery(id+"F27.opExtrude","CAP_EDGE",EDGE,{"disambiguationData":[OSD([sQuery(id+"F26.wireOp",EDGE,"E62.left")])],"isStart":true})});
            fillet(context, id + "F37", {"entities" : qUnion([Q0, Q1, Q2, Q3]), "radius" : 0.5 * mm, "tangentPropagation" : true, "allowEdgeOverflow" : false});
        }
    });
